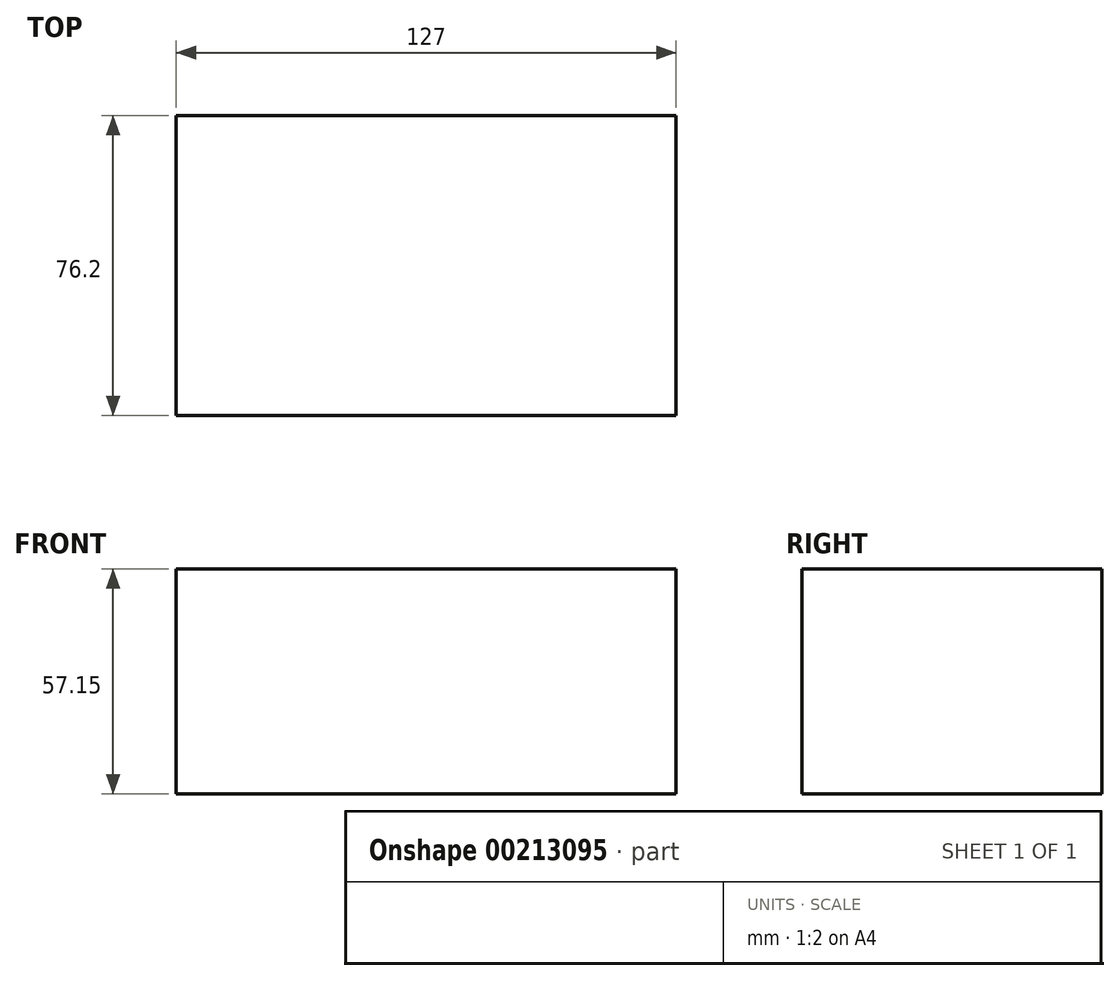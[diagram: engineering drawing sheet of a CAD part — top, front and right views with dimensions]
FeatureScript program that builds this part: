
annotation { "Feature Type Name" : "Feature", "Feature Type Description" : "" }
export const myFeature = defineFeature(function(context is Context, id is Id, definition is map)
    precondition{}
    {
        {
            var Q0;
            Q0=qCreatedBy(makeId("Top.planeOp"),FACE);
            var sketch = newSketch(context, id + "F0", { "sketchPlane" : qUnion([Q0])});
            skLineSegment(sketch, "E0.bottom", {"start": v(0, 0) * mm, "end": v(127, 0) * mm});
            skLineSegment(sketch, "E0.top", {"start": v(0, 76.2) * mm, "end": v(127, 76.2) * mm});
            skLineSegment(sketch, "E0.left", {"start": v(0, 0) * mm, "end": v(0, 76.2) * mm});
            skLineSegment(sketch, "E0.right", {"start": v(127, 0) * mm, "end": v(127, 76.2) * mm});
            skSolve(sketch);
        }
        {
            var Q0;
            Q0 = qSketchRegion(id + "F0", true);
            extrude(context, id + "F1", {"entities" : qUnion([Q0]), "depth" : 57.15 * mm});
        }
    });
